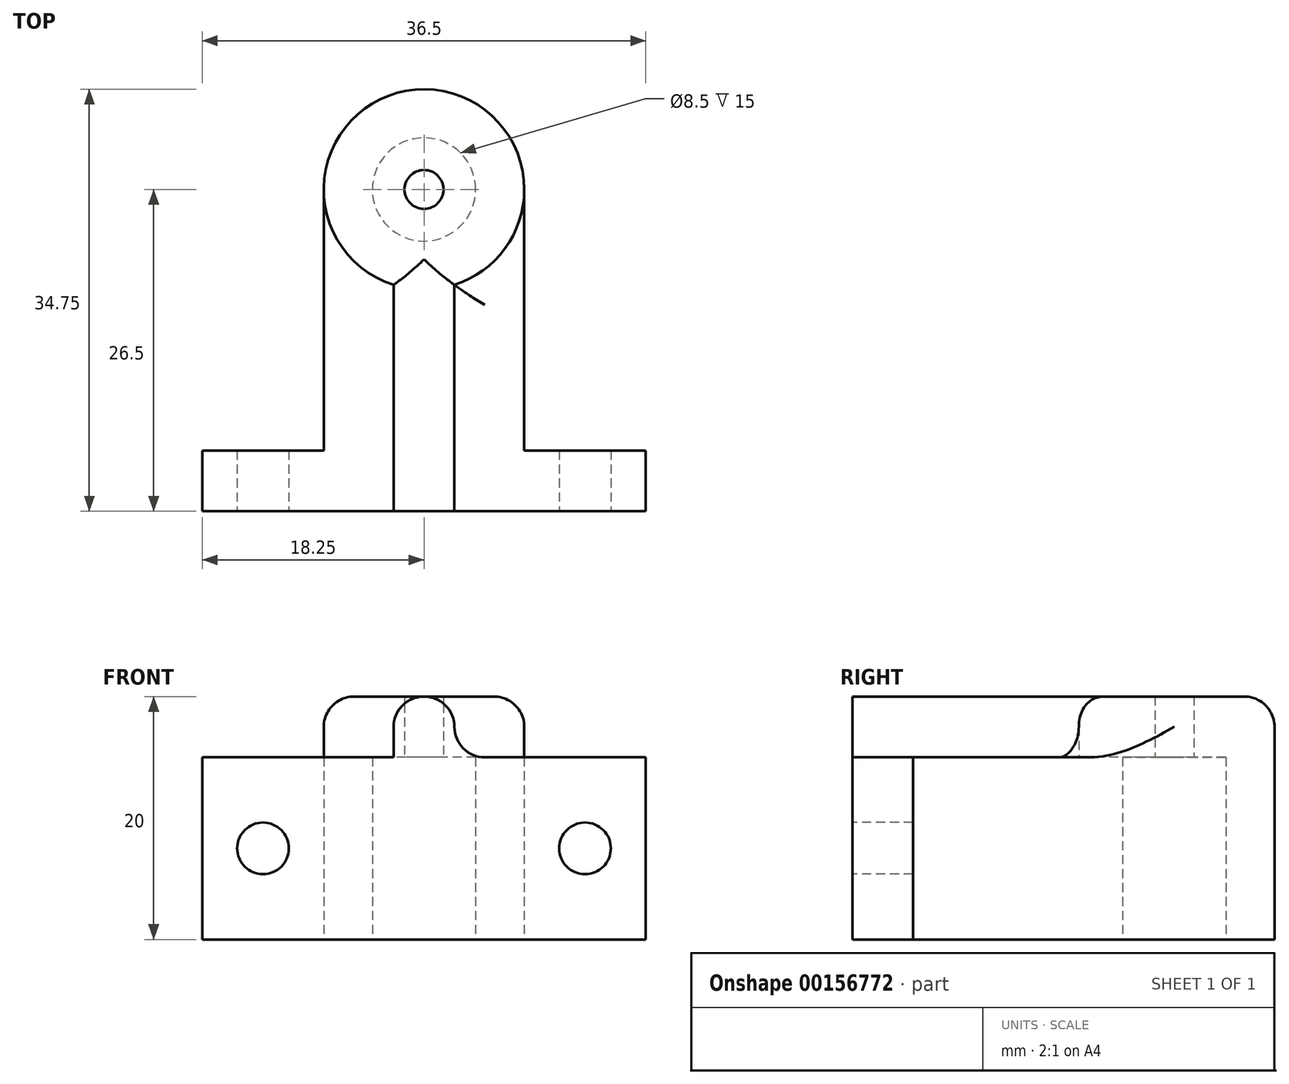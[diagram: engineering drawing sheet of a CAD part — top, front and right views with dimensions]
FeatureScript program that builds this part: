
annotation { "Feature Type Name" : "Feature", "Feature Type Description" : "" }
export const myFeature = defineFeature(function(context is Context, id is Id, definition is map)
    precondition{}
    {
        {
            var Q0;
            Q0=qCreatedBy(makeId("Top.planeOp"),FACE);
            var sketch = newSketch(context, id + "F0", { "sketchPlane" : qUnion([Q0])});
            skCircle(sketch, "E0", {"center": v(0, 0) * mm, "radius": 4.25 * mm});
            skArc(sketch, "E1", {"start": v(8.25, 0) * mm, "mid": v(0, 8.25) * mm, "end": v(-8.25, 0) * mm});
            skLineSegment(sketch, "E2", {"start": v(-8.25, 0) * mm, "end": v(-8.25, -21.5) * mm});
            skLineSegment(sketch, "E3", {"start": v(-8.25, -21.5) * mm, "end": v(-18.25, -21.5) * mm});
            skLineSegment(sketch, "E4", {"start": v(-18.25, -21.5) * mm, "end": v(-18.25, -26.5) * mm});
            skLineSegment(sketch, "E5", {"start": v(-18.25, -26.5) * mm, "end": v(0, -26.5) * mm});
            skLineSegment(sketch, "E6.MirrorCS", {"start": v(8.25, 0) * mm, "end": v(8.25, -21.5) * mm});
            skLineSegment(sketch, "E7.MirrorCS", {"start": v(8.25, -21.5) * mm, "end": v(18.25, -21.5) * mm});
            skLineSegment(sketch, "E8.MirrorCS", {"start": v(18.25, -21.5) * mm, "end": v(18.25, -26.5) * mm});
            skLineSegment(sketch, "E9.MirrorCS", {"start": v(18.25, -26.5) * mm, "end": v(0, -26.5) * mm});
            skSolve(sketch);
        }
        {
            var Q0;
            Q0=qSketchRegion(id+"F0",true);
            extrude(context, id + "F1", {"entities" : qUnion([Q0]), "depth" : 15 * mm});
        }
        {
            var Q0;
            Q0=makeQuery(id+"F1.opExtrude","SWEPT_FACE",FACE,{"disambiguationData":[OSD([sQuery(id+"F0.wireOp",EDGE,"E5"),sQuery(id+"F0.wireOp",EDGE,"E9.MirrorCS")])]});
            var sketch = newSketch(context, id + "F2", { "sketchPlane" : qUnion([Q0])});
            skCircle(sketch, "E10", {"center": v(-13.25, 7.5) * mm, "radius": 2.12 * mm});
            skCircle(sketch, "E11", {"center": v(13.25, 7.5) * mm, "radius": 2.12 * mm});
            skSolve(sketch);
        }
        {
            var Q0;
            Q0=qSketchRegion(id+"F2",true);
            extrude(context, id + "F3", {"entities" : qUnion([Q0]), "operationType" : NewBodyOperationType.REMOVE, "endBound" : BoundingType.THROUGH_ALL, "oppositeDirection" : true, "depth" : 25 * mm});
        }
        {
            var Q0;
            Q0=makeQuery(id+"F1.opExtrude","CAP_FACE",FACE,{"disambiguationData":[OSD([sQuery(id+"F0.wireOp",EDGE,"E0"),sQuery(id+"F0.wireOp",EDGE,"E1"),sQuery(id+"F0.wireOp",EDGE,"E2"),sQuery(id+"F0.wireOp",EDGE,"E3"),sQuery(id+"F0.wireOp",EDGE,"E4"),sQuery(id+"F0.wireOp",EDGE,"E5"),sQuery(id+"F0.wireOp",EDGE,"E6.MirrorCS"),sQuery(id+"F0.wireOp",EDGE,"E7.MirrorCS"),sQuery(id+"F0.wireOp",EDGE,"E8.MirrorCS"),sQuery(id+"F0.wireOp",EDGE,"E9.MirrorCS")])],"isStart":false});
            var sketch = newSketch(context, id + "F4", { "sketchPlane" : qUnion([Q0])});
            skArc(sketch, "E12", {"start": v(8.25, 0) * mm, "mid": v(0, 8.25) * mm, "end": v(-8.25, 0) * mm});
            skCircle(sketch, "E13", {"center": v(0, 0) * mm, "radius": 1.6 * mm});
            skArc(sketch, "E14", {"start": v(-8.25, 0) * mm, "mid": v(-6.66, -4.87) * mm, "end": v(-2.5, -7.86) * mm});
            skArc(sketch, "E15", {"start": v(8.25, 0) * mm, "mid": v(6.66, -4.87) * mm, "end": v(2.5, -7.86) * mm});
            skLineSegment(sketch, "E16", {"start": v(-2.5, -7.86) * mm, "end": v(-2.5, -26.5) * mm});
            skLineSegment(sketch, "E17", {"start": v(-2.5, -26.5) * mm, "end": v(2.5, -26.5) * mm});
            skLineSegment(sketch, "E18", {"start": v(2.5, -26.5) * mm, "end": v(2.5, -7.86) * mm});
            skSolve(sketch);
        }
        {
            var Q0;
            Q0=qSketchRegion(id+"F4",true);
            extrude(context, id + "F5", {"entities" : qUnion([Q0]), "operationType" : NewBodyOperationType.ADD, "depth" : 5 * mm});
        }
        {
            var Q0;
            Q0=makeQuery(id+"F5.opExtrude","CAP_EDGE",EDGE,{"disambiguationData":[OSD([sQuery(id+"F4.wireOp",EDGE,"E12"),sQuery(id+"F4.wireOp",EDGE,"E14"),sQuery(id+"F4.wireOp",EDGE,"E15")])],"isStart":false});
            var Q1;
            {var subQ0=sQuery(id+"F0.wireOp",EDGE,"E2");var subQ1=sQuery(id+"F4.wireOp",EDGE,"E15");var subQ2=sQuery(id+"F4.wireOp",EDGE,"E14");var subQ3=sQuery(id+"F4.wireOp",EDGE,"E12");Q1=makeQuery(id+"F5.boolean.opBoolean","SPLIT",EDGE,{"disambiguationData":[TD([makeQuery(id+"F1.opExtrude","SWEPT_FACE",FACE,{"disambiguationData":[OSD([subQ0])]})])],"derivedFrom":makeQuery(id+"F5.opExtrude","CAP_EDGE",EDGE,{"disambiguationData":[OSD([subQ3,subQ2,subQ1])],"isStart":true})});}
            var Q2;
            Q2=makeQuery(id+"F5.opExtrude","CAP_EDGE",EDGE,{"disambiguationData":[OSD([sQuery(id+"F4.wireOp",EDGE,"E16")])],"isStart":true});
            var Q3;
            Q3=makeQuery(id+"F5.opExtrude","CAP_EDGE",EDGE,{"disambiguationData":[OSD([sQuery(id+"F4.wireOp",EDGE,"E16")])],"isStart":false});
            var Q4;
            {var subQ0=sQuery(id+"F4.wireOp",EDGE,"E15");var subQ1=sQuery(id+"F4.wireOp",EDGE,"E14");var subQ2=sQuery(id+"F4.wireOp",EDGE,"E12");var subQ3=sQuery(id+"F0.wireOp",EDGE,"E6.MirrorCS");Q4=makeQuery(id+"F5.boolean.opBoolean","SPLIT",EDGE,{"disambiguationData":[TD([makeQuery(id+"F1.opExtrude","SWEPT_FACE",FACE,{"disambiguationData":[OSD([subQ3])]})])],"derivedFrom":makeQuery(id+"F5.opExtrude","CAP_EDGE",EDGE,{"disambiguationData":[OSD([subQ2,subQ1,subQ0])],"isStart":true})});}
            var Q5;
            Q5=makeQuery(id+"F5.opExtrude","CAP_EDGE",EDGE,{"disambiguationData":[OSD([sQuery(id+"F4.wireOp",EDGE,"E18")])],"isStart":false});
            var Q6;
            Q6=makeQuery(id+"F5.opExtrude","CAP_EDGE",EDGE,{"disambiguationData":[OSD([sQuery(id+"F4.wireOp",EDGE,"E18")])],"isStart":true});
            fillet(context, id + "F6", {"entities" : qUnion([Q0, Q1, Q2, Q3, Q4, Q5, Q6]), "radius" : 2.5 * mm, "tangentPropagation" : true, "allowEdgeOverflow" : false});
        }
    });
